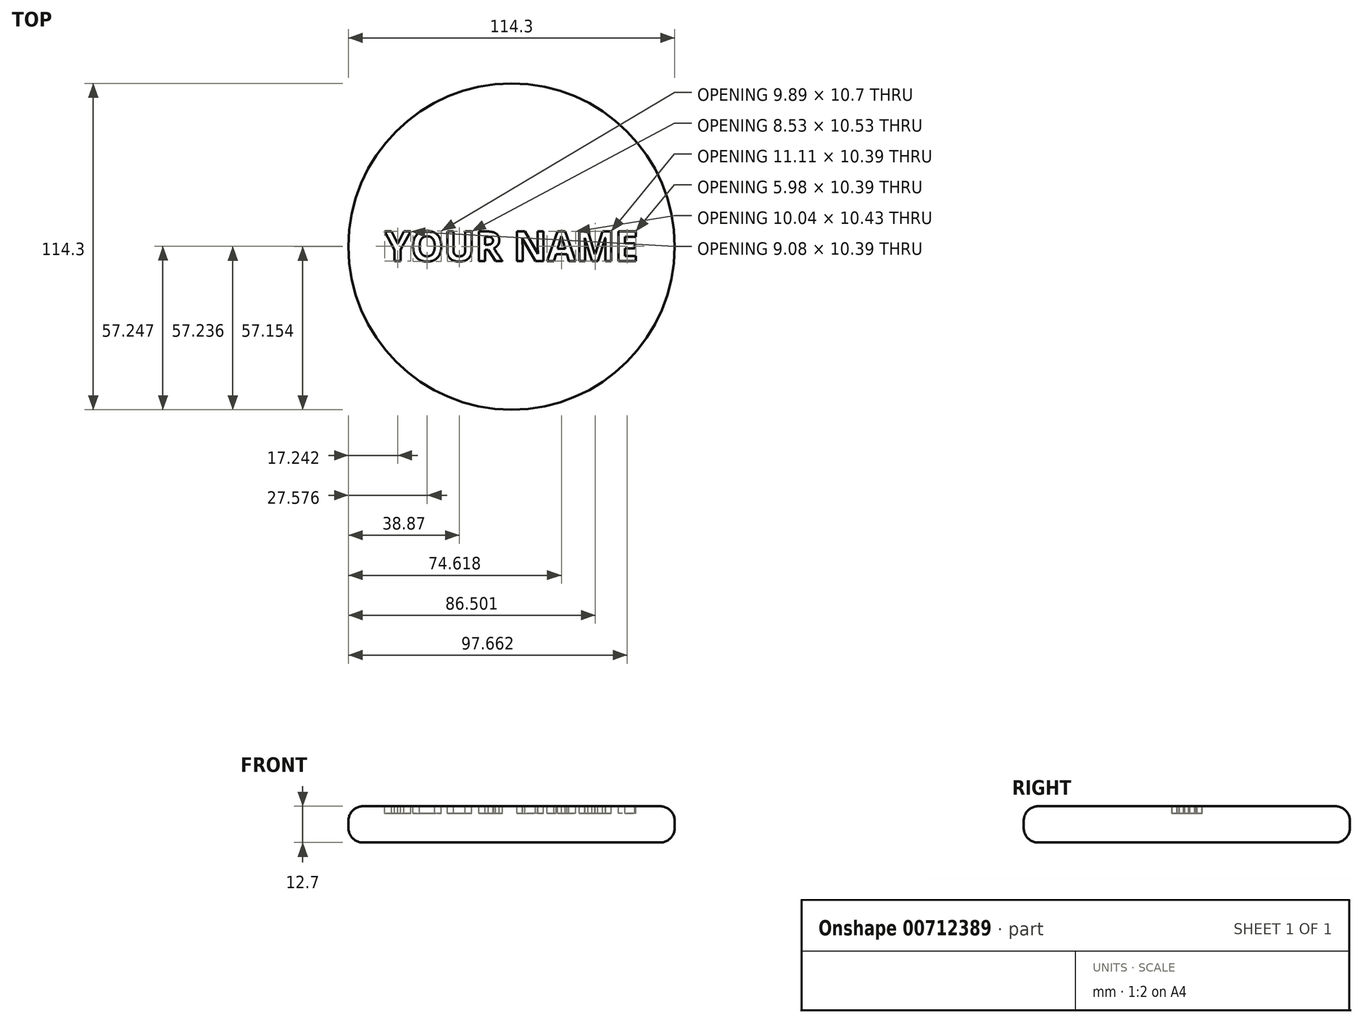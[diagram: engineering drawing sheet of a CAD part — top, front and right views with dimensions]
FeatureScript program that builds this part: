
annotation { "Feature Type Name" : "Feature", "Feature Type Description" : "" }
export const myFeature = defineFeature(function(context is Context, id is Id, definition is map)
    precondition{}
    {
        {
            var Q0;
            Q0=qCreatedBy(makeId("Top.planeOp"),FACE);
            var sketch = newSketch(context, id + "F0", { "sketchPlane" : qUnion([Q0])});
            skCircle(sketch, "E0", {"center": v(0, 0) * mm, "radius": 57.15 * mm});
            skSolve(sketch);
        }
        {
            var Q0;
            Q0=qSketchRegion(id+"F0",true);
            extrude(context, id + "F1", {"entities" : qUnion([Q0]), "depth" : 12.7 * mm, "offsetDistance" : 25.4 * mm});
        }
        {
            var Q0;
            Q0=makeQuery(id+"F1.opExtrude","CAP_EDGE",EDGE,{"disambiguationData":[OSD([sQuery(id+"F0.wireOp",EDGE,"E0")])],"isStart":false});
            var Q1;
            Q1=makeQuery(id+"F1.opExtrude","CAP_EDGE",EDGE,{"disambiguationData":[OSD([sQuery(id+"F0.wireOp",EDGE,"E0")])],"isStart":true});
            fillet(context, id + "F2", {"entities" : qUnion([Q0, Q1]), "radius" : 5.08 * mm, "tangentPropagation" : true, "allowEdgeOverflow" : false});
        }
        {
            var Q0;
            Q0=makeQuery(id+"F1.opExtrude","CAP_FACE",FACE,{"disambiguationData":[OSD([sQuery(id+"F0.wireOp",EDGE,"E0")])],"isStart":false});
            var sketch = newSketch(context, id + "F3", { "sketchPlane" : qUnion([Q0])});
            skText(sketch, "E1", { "text": "YOUR NAME\n", "fontName": "OpenSans-Bold.ttf"});
            skLineSegment(sketch, "E2", {"start": v(0, 52.07) * mm, "end": v(0, -52.07) * mm, "construction": true});
            skPoint(sketch, "E3.endSnap0", {"position": v(-44.45, 0.12) * mm});
            skLineSegment(sketch, "E4", {"start": v(-52.07, 0.12) * mm, "end": v(52.07, 0.12) * mm, "construction": true});
            skLineSegment(sketch, "E5", {"start": v(0, 5.36) * mm, "end": v(0, -5.12) * mm, "construction": true});
            skText(sketch, "E6", { "text": "RUBIN", "fontName": "OpenSans-Bold.ttf"});
            skLineSegment(sketch, "E7", {"start": v(-228.75, -76.6) * mm, "end": v(-228.75, -93.7) * mm, "construction": true});
            skPoint(sketch, "E8", {"position": v(0, 0.12) * mm});
            const initialGuessF3  = {"E1": [-0.04445, -0.00512, 1, 0, 0.01048], "E6": [-0.26685, -0.0937, 1, 0, 0.0171]};
            skSetInitialGuess(sketch, initialGuessF3);
            skSolve(sketch);
        }
        {
            var Q0;
            Q0=qSketchRegion(id+"F3",true);
            extrude(context, id + "F4", {"entities" : qUnion([Q0]), "operationType" : NewBodyOperationType.REMOVE, "oppositeDirection" : true, "depth" : 2.54 * mm, "offsetDistance" : 25.4 * mm});
        }
    });
